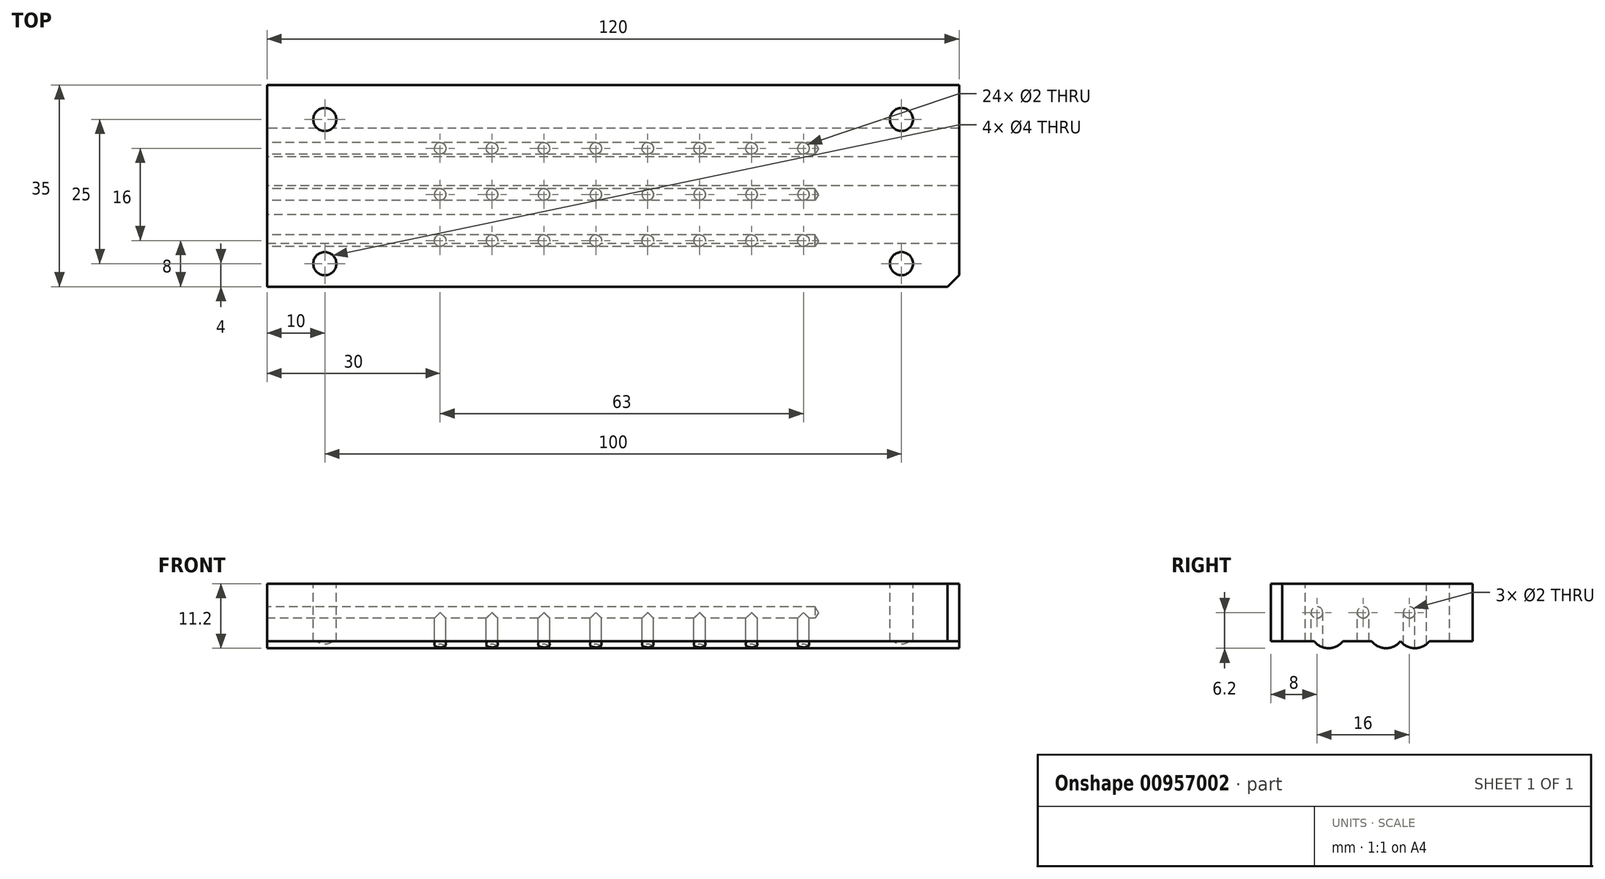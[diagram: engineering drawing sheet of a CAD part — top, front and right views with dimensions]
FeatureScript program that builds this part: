
annotation { "Feature Type Name" : "Feature", "Feature Type Description" : "" }
export const myFeature = defineFeature(function(context is Context, id is Id, definition is map)
    precondition{}
    {
        {
            var Q0;
            Q0=qCreatedBy(makeId("Top.planeOp"),FACE);
            cPlane(context, id + "F0", {"entities" : qUnion([Q0]), "cplaneType" : CPlaneType.OFFSET, "offset" : 5 * mm, "width" : 150 * mm, "height" : 150 * mm});
        }
        {
            var Q0;
            Q0=qCreatedBy(makeId("Right.planeOp"),FACE);
            var sketch = newSketch(context, id + "F1", { "sketchPlane" : qUnion([Q0])});
            skLineSegment(sketch, "E0.bottom", {"start": v(0, 0) * mm, "end": v(7.5, 0) * mm});
            skLineSegment(sketch, "E0.top", {"start": v(0, 10) * mm, "end": v(35, 10) * mm});
            skLineSegment(sketch, "E0.left", {"start": v(0, 0) * mm, "end": v(0, 10) * mm});
            skLineSegment(sketch, "E0.right", {"start": v(35, 0) * mm, "end": v(35, 10) * mm});
            skArc(sketch, "E1", {"start": v(7.5, 0) * mm, "mid": v(10, -1.2) * mm, "end": v(12.5, 0) * mm});
            skArc(sketch, "E2.1.0.0", {"start": v(17.5, 0) * mm, "mid": v(20, -1.2) * mm, "end": v(22.5, 0) * mm});
            skLineSegment(sketch, "E2.direction1", {"start": v(12.5, 0) * mm, "end": v(17.5, 0) * mm, "construction": true});
            skArc(sketch, "E3.1.0.0", {"start": v(22.5, 0) * mm, "mid": v(25, -1.2) * mm, "end": v(27.5, 0) * mm});
            skLineSegment(sketch, "E3.direction1", {"start": v(22.5, 0) * mm, "end": v(22.5, 0) * mm, "construction": true});
            skLineSegment(sketch, "E4.trimOffspring", {"start": v(12.5, 0) * mm, "end": v(17.5, 0) * mm});
            skLineSegment(sketch, "E5.trimOffspring", {"start": v(22.5, 0) * mm, "end": v(22.5, 0) * mm});
            skLineSegment(sketch, "E6.trimOffspring", {"start": v(27.5, 0) * mm, "end": v(35, 0) * mm});
            skSolve(sketch);
        }
        {
            var Q0;
            Q0=makeQuery(id+"F1.imprint","IMPRINT",FACE,{"disambiguationData":[TD([[makeQuery(id+"F1.imprint","IMPRINT",EDGE,{"derivedFrom":sQuery(id+"F1.wireOp",EDGE,"E0.bottom")}),1.0]])]});
            extrude(context, id + "F2", {"entities" : qUnion([Q0]), "depth" : 120 * mm, "offsetDistance" : 25 * mm});
        }
        {
            var Q0;
            Q0=makeQuery(id+"F2.opExtrude","CAP_EDGE",EDGE,{"disambiguationData":[OSD([sQuery(id+"F1.wireOp",EDGE,"E0.left")])],"isStart":false});
            chamfer(context, id + "F3", {"entities" : qUnion([Q0]), "width" : 2 * mm, "tangentPropagation" : true});
        }
        {
            var Q0;
            Q0=qCreatedBy(makeId("Right.planeOp"),FACE);
            var sketch = newSketch(context, id + "F4", { "sketchPlane" : qUnion([Q0])});
            skPoint(sketch, "E7", {"position": v(8, 5) * mm});
            skPoint(sketch, "E8", {"position": v(16, 5) * mm});
            skPoint(sketch, "E9", {"position": v(24, 5) * mm});
            skSolve(sketch);
        }
        {
            var Q0;
            Q0=sQuery(id+"F4.wireOp",VERTEX,"E9");
            var Q1;
            Q1=sQuery(id+"F4.wireOp",VERTEX,"E8");
            var Q2;
            Q2=sQuery(id+"F4.wireOp",VERTEX,"E7");
            var Q3;
            Q3=makeQuery(id+"F2.opExtrude","SWEPT_BODY",BODY,{"disambiguationData":[OSD([sQuery(id+"F1.wireOp",EDGE,"E0.bottom"),sQuery(id+"F1.wireOp",EDGE,"E0.top"),sQuery(id+"F1.wireOp",EDGE,"E0.left"),sQuery(id+"F1.wireOp",EDGE,"E0.right")])]});
            hole(context, id + "F5", {"style" : HoleStyle.SIMPLE, "endStyle" : HoleEndStyle.BLIND, "oppositeDirection" : true, "standardTappedOrClearance" : lookupTablePath({ "standard" : "ISO", "size" : "2", "type" : "Drilled" }), "standardBlindInLast" : lookupTablePath({ "standard" : "ISO", "size" : "2", "type" : "Drilled" }), "holeDiameter" : 2 * mm, "majorDiameter" : 5 * mm, "holeDepth" : 95 * mm, "isTappedThrough" : true, "tappedDepth" : 12 * mm, "tapClearance" : 3, "locations" : qUnion([Q0, Q1, Q2]), "scope" : qUnion([Q3])});
        }
        {
            var Q0;
            Q0=qCreatedBy(id+"F0.planeOp",FACE);
            var sketch = newSketch(context, id + "F6", { "sketchPlane" : qUnion([Q0])});
            skPoint(sketch, "E10", {"position": v(30, 8) * mm});
            skPoint(sketch, "E11", {"position": v(30, 16) * mm});
            skPoint(sketch, "E12", {"position": v(30, 24) * mm});
            skPoint(sketch, "E13.1.0.0", {"position": v(39, 24) * mm});
            skPoint(sketch, "E13.1.0.1", {"position": v(39, 16) * mm});
            skPoint(sketch, "E13.1.0.2", {"position": v(39, 8) * mm});
            skPoint(sketch, "E13.2.0.0", {"position": v(48, 24) * mm});
            skPoint(sketch, "E13.2.0.1", {"position": v(48, 16) * mm});
            skPoint(sketch, "E13.2.0.2", {"position": v(48, 8) * mm});
            skPoint(sketch, "E13.3.0.0", {"position": v(57, 24) * mm});
            skPoint(sketch, "E13.3.0.1", {"position": v(57, 16) * mm});
            skPoint(sketch, "E13.3.0.2", {"position": v(57, 8) * mm});
            skPoint(sketch, "E13.4.0.0", {"position": v(66, 24) * mm});
            skPoint(sketch, "E13.4.0.1", {"position": v(66, 16) * mm});
            skPoint(sketch, "E13.4.0.2", {"position": v(66, 8) * mm});
            skPoint(sketch, "E13.5.0.0", {"position": v(75, 24) * mm});
            skPoint(sketch, "E13.5.0.1", {"position": v(75, 16) * mm});
            skPoint(sketch, "E13.5.0.2", {"position": v(75, 8) * mm});
            skPoint(sketch, "E13.6.0.0", {"position": v(84, 24) * mm});
            skPoint(sketch, "E13.6.0.1", {"position": v(84, 16) * mm});
            skPoint(sketch, "E13.6.0.2", {"position": v(84, 8) * mm});
            skPoint(sketch, "E13.7.0.0", {"position": v(93, 24) * mm});
            skPoint(sketch, "E13.7.0.1", {"position": v(93, 16) * mm});
            skPoint(sketch, "E13.7.0.2", {"position": v(93, 8) * mm});
            skLineSegment(sketch, "E13.direction1", {"start": v(20, 23) * mm, "end": v(29, 23) * mm, "construction": true});
            skSolve(sketch);
        }
        {
            var Q0;
            Q0=sQuery(id+"F6.wireOp",VERTEX,"E12");
            var Q1;
            Q1=sQuery(id+"F6.wireOp",VERTEX,"E11");
            var Q2;
            Q2=sQuery(id+"F6.wireOp",VERTEX,"E10");
            var Q3;
            Q3=sQuery(id+"F6.wireOp",VERTEX,"E13.1.0.2");
            var Q4;
            Q4=sQuery(id+"F6.wireOp",VERTEX,"E13.1.0.1");
            var Q5;
            Q5=sQuery(id+"F6.wireOp",VERTEX,"E13.1.0.0");
            var Q6;
            Q6=sQuery(id+"F6.wireOp",VERTEX,"E13.2.0.2");
            var Q7;
            Q7=sQuery(id+"F6.wireOp",VERTEX,"E13.2.0.1");
            var Q8;
            Q8=sQuery(id+"F6.wireOp",VERTEX,"E13.2.0.0");
            var Q9;
            Q9=sQuery(id+"F6.wireOp",VERTEX,"E13.3.0.0");
            var Q10;
            Q10=sQuery(id+"F6.wireOp",VERTEX,"E13.3.0.1");
            var Q11;
            Q11=sQuery(id+"F6.wireOp",VERTEX,"E13.3.0.2");
            var Q12;
            Q12=sQuery(id+"F6.wireOp",VERTEX,"E13.4.0.2");
            var Q13;
            Q13=sQuery(id+"F6.wireOp",VERTEX,"E13.4.0.1");
            var Q14;
            Q14=sQuery(id+"F6.wireOp",VERTEX,"E13.4.0.0");
            var Q15;
            Q15=sQuery(id+"F6.wireOp",VERTEX,"E13.5.0.0");
            var Q16;
            Q16=sQuery(id+"F6.wireOp",VERTEX,"E13.5.0.1");
            var Q17;
            Q17=sQuery(id+"F6.wireOp",VERTEX,"E13.5.0.2");
            var Q18;
            Q18=sQuery(id+"F6.wireOp",VERTEX,"E13.6.0.2");
            var Q19;
            Q19=sQuery(id+"F6.wireOp",VERTEX,"E13.6.0.1");
            var Q20;
            Q20=sQuery(id+"F6.wireOp",VERTEX,"E13.6.0.0");
            var Q21;
            Q21=sQuery(id+"F6.wireOp",VERTEX,"E13.7.0.0");
            var Q22;
            Q22=sQuery(id+"F6.wireOp",VERTEX,"E13.7.0.1");
            var Q23;
            Q23=sQuery(id+"F6.wireOp",VERTEX,"E13.7.0.2");
            var Q24;
            Q24=makeQuery(id+"F2.opExtrude","SWEPT_BODY",BODY,{"disambiguationData":[OSD([sQuery(id+"F1.wireOp",EDGE,"E0.bottom"),sQuery(id+"F1.wireOp",EDGE,"E0.top"),sQuery(id+"F1.wireOp",EDGE,"E0.left"),sQuery(id+"F1.wireOp",EDGE,"E0.right")])]});
            hole(context, id + "F7", {"style" : HoleStyle.SIMPLE, "endStyle" : HoleEndStyle.BLIND, "standardTappedOrClearance" : lookupTablePath({ "standard" : "ISO", "size" : "2", "type" : "Drilled" }), "standardBlindInLast" : lookupTablePath({ "standard" : "ISO", "size" : "2", "type" : "Drilled" }), "holeDiameter" : 2 * mm, "majorDiameter" : 5 * mm, "holeDepth" : 10 * mm, "isTappedThrough" : true, "tappedDepth" : 12 * mm, "tapClearance" : 3, "locations" : qUnion([Q0, Q1, Q2, Q3, Q4, Q5, Q6, Q7, Q8, Q9, Q10, Q11, Q12, Q13, Q14, Q15, Q16, Q17, Q18, Q19, Q20, Q21, Q22, Q23]), "scope" : qUnion([Q24])});
        }
        {
            var Q0;
            Q0=makeQuery(id+"F2.opExtrude","SWEPT_FACE",FACE,{"disambiguationData":[OSD([sQuery(id+"F1.wireOp",EDGE,"E0.top")])]});
            var sketch = newSketch(context, id + "F8", { "sketchPlane" : qUnion([Q0])});
            skPoint(sketch, "E14", {"position": v(10, 29) * mm});
            skPoint(sketch, "E15", {"position": v(10, 4) * mm});
            skPoint(sketch, "E16.1.0.0", {"position": v(110, 29) * mm});
            skPoint(sketch, "E16.1.0.1", {"position": v(110, 4) * mm});
            skLineSegment(sketch, "E16.direction1", {"start": v(10, 29) * mm, "end": v(110, 29) * mm, "construction": true});
            skSolve(sketch);
        }
        {
            var Q0;
            Q0=sQuery(id+"F8.wireOp",VERTEX,"E14");
            var Q1;
            Q1=sQuery(id+"F8.wireOp",VERTEX,"E15");
            var Q2;
            Q2=sQuery(id+"F8.wireOp",VERTEX,"E16.1.0.1");
            var Q3;
            Q3=sQuery(id+"F8.wireOp",VERTEX,"E16.1.0.0");
            var Q4;
            Q4=makeQuery(id+"F2.opExtrude","SWEPT_BODY",BODY,{"disambiguationData":[OSD([sQuery(id+"F1.wireOp",EDGE,"E0.bottom"),sQuery(id+"F1.wireOp",EDGE,"E0.top"),sQuery(id+"F1.wireOp",EDGE,"E0.left"),sQuery(id+"F1.wireOp",EDGE,"E0.right"),sQuery(id+"F1.wireOp",EDGE,"E1"),sQuery(id+"F1.wireOp",EDGE,"E2.1.0.0"),sQuery(id+"F1.wireOp",EDGE,"E3.1.0.0"),sQuery(id+"F1.wireOp",EDGE,"E4.trimOffspring"),sQuery(id+"F1.wireOp",EDGE,"E5.trimOffspring"),sQuery(id+"F1.wireOp",EDGE,"E6.trimOffspring")])]});
            hole(context, id + "F9", {"style" : HoleStyle.SIMPLE, "endStyle" : HoleEndStyle.THROUGH, "standardTappedOrClearance" : lookupTablePath({ "standard" : "ISO", "size" : "4", "type" : "Drilled" }), "standardBlindInLast" : lookupTablePath({ "standard" : "ISO", "size" : "4", "type" : "Drilled" }), "holeDiameter" : 4 * mm, "majorDiameter" : 5 * mm, "isTappedThrough" : true, "tappedDepth" : 12 * mm, "tapClearance" : 3, "locations" : qUnion([Q0, Q1, Q2, Q3]), "scope" : qUnion([Q4])});
        }
    });
